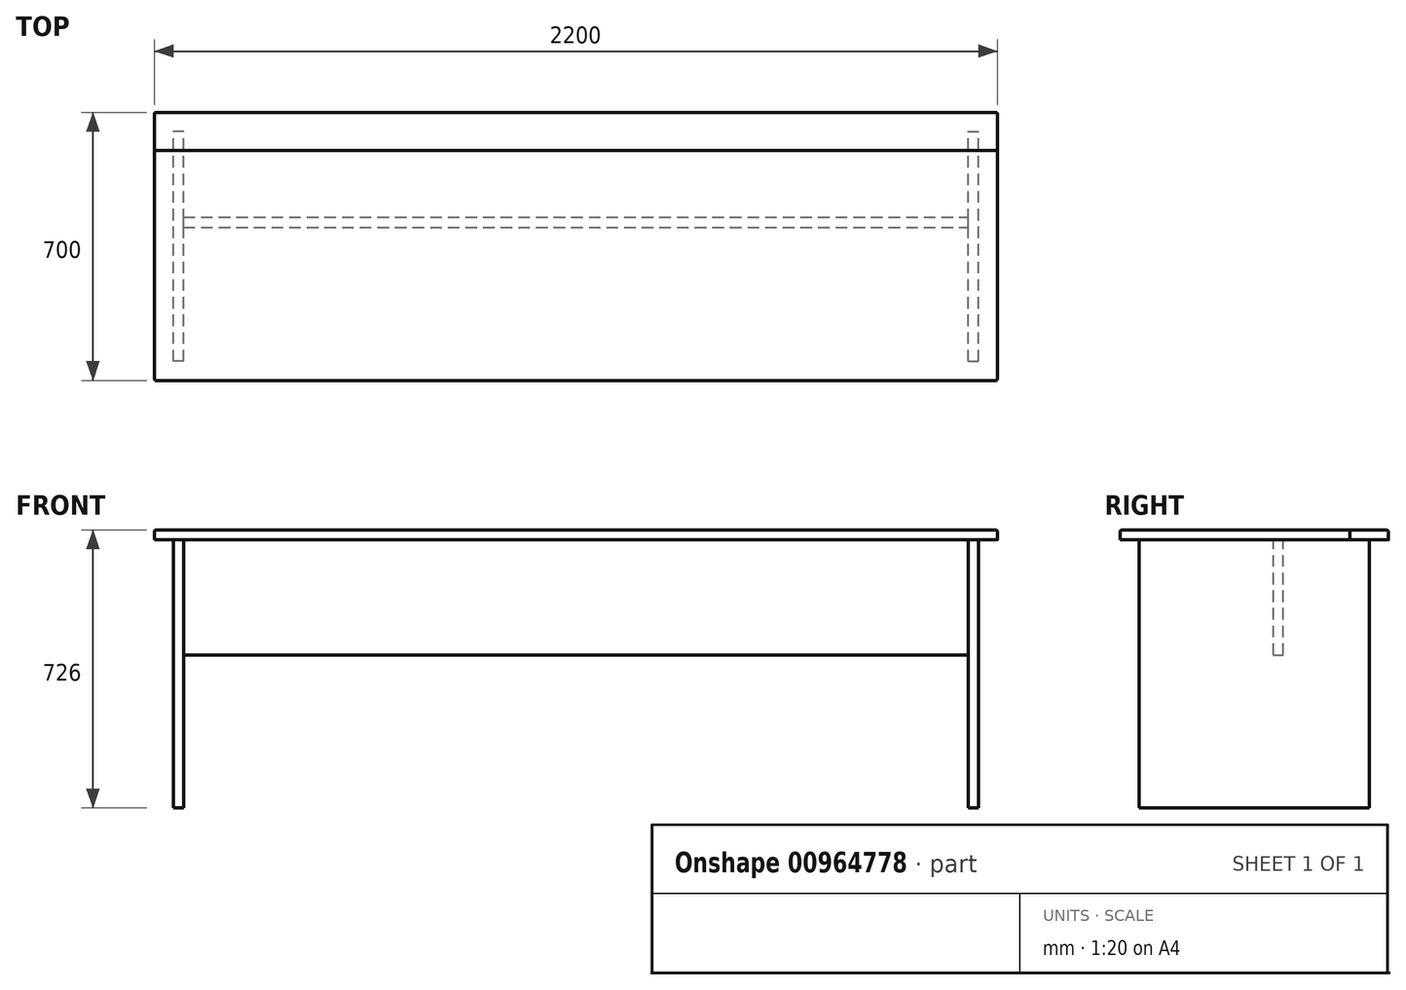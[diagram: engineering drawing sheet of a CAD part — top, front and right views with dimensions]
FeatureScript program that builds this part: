
annotation { "Feature Type Name" : "Feature", "Feature Type Description" : "" }
export const myFeature = defineFeature(function(context is Context, id is Id, definition is map)
    precondition{}
    {
        {
            var Q0;
            Q0=qCreatedBy(makeId("Top.planeOp"),FACE);
            var sketch = newSketch(context, id + "F0", { "sketchPlane" : qUnion([Q0])});
            skLineSegment(sketch, "E0.bottom", {"start": v(0, 0) * mm, "end": v(2200, 0) * mm});
            skLineSegment(sketch, "E0.top", {"start": v(0, 600) * mm, "end": v(2200, 600) * mm});
            skLineSegment(sketch, "E0.left", {"start": v(0, 0) * mm, "end": v(0, 600) * mm});
            skLineSegment(sketch, "E0.right", {"start": v(2200, 0) * mm, "end": v(2200, 600) * mm});
            skLineSegment(sketch, "E1.top", {"start": v(0, 700) * mm, "end": v(2200, 700) * mm});
            skLineSegment(sketch, "E1.left", {"start": v(0, 600) * mm, "end": v(0, 700) * mm});
            skLineSegment(sketch, "E1.right", {"start": v(2200, 600) * mm, "end": v(2200, 700) * mm});
            skSolve(sketch);
        }
        {
            var Q0;
            Q0=makeQuery(id+"F0.imprint","IMPRINT",FACE,{"disambiguationData":[TD([[makeQuery(id+"F0.imprint","IMPRINT",EDGE,{"derivedFrom":sQuery(id+"F0.wireOp",EDGE,"E0.bottom")}),1.0]])]});
            extrude(context, id + "F1", {"entities" : qUnion([Q0]), "oppositeDirection" : true, "depth" : 26 * mm, "offsetDistance" : 25 * mm});
        }
        {
            var Q0;
            Q0=makeQuery(id+"F0.imprint","IMPRINT",FACE,{"disambiguationData":[TD([[makeQuery(id+"F0.imprint","IMPRINT",EDGE,{"derivedFrom":sQuery(id+"F0.wireOp",EDGE,"E0.top")}),1.0]])]});
            extrude(context, id + "F2", {"entities" : qUnion([Q0]), "oppositeDirection" : true, "depth" : 26 * mm, "offsetDistance" : 25 * mm});
        }
        {
            var Q0;
            Q0=makeQuery(id+"F1.opExtrude","CAP_FACE",FACE,{"disambiguationData":[OSD([sQuery(id+"F0.wireOp",EDGE,"E0.bottom"),sQuery(id+"F0.wireOp",EDGE,"E0.left"),sQuery(id+"F0.wireOp",EDGE,"E0.right"),sQuery(id+"F0.wireOp",EDGE,"E0.top")])],"isStart":false});
            var sketch = newSketch(context, id + "F3", { "sketchPlane" : qUnion([Q0])});
            skLineSegment(sketch, "E2.0.0", {"start": v(0, -600) * mm, "end": v(2200, -600) * mm, "construction": true});
            skLineSegment(sketch, "E2.0.1", {"start": v(0, 0) * mm, "end": v(0, -600) * mm, "construction": true});
            skLineSegment(sketch, "E2.0.2", {"start": v(2200, 0) * mm, "end": v(0, 0) * mm, "construction": true});
            skLineSegment(sketch, "E2.0.3", {"start": v(2200, -600) * mm, "end": v(2200, 0) * mm, "construction": true});
            skLineSegment(sketch, "E3.0.0", {"start": v(0, -700) * mm, "end": v(2200, -700) * mm, "construction": true});
            skLineSegment(sketch, "E3.0.1", {"start": v(0, -600) * mm, "end": v(0, -700) * mm, "construction": true});
            skLineSegment(sketch, "E3.0.2", {"start": v(2200, -600) * mm, "end": v(0, -600) * mm, "construction": true});
            skLineSegment(sketch, "E3.0.3", {"start": v(2200, -700) * mm, "end": v(2200, -600) * mm, "construction": true});
            skLineSegment(sketch, "E4.bottom", {"start": v(76, -650) * mm, "end": v(50, -650) * mm});
            skLineSegment(sketch, "E4.top", {"start": v(76, -50) * mm, "end": v(50, -50) * mm});
            skLineSegment(sketch, "E4.left", {"start": v(50, -50) * mm, "end": v(50, -650) * mm});
            skLineSegment(sketch, "E4.right", {"start": v(76, -50) * mm, "end": v(76, -650) * mm});
            skLineSegment(sketch, "E5.bottom", {"start": v(2124, -650) * mm, "end": v(2150, -650) * mm});
            skLineSegment(sketch, "E5.top", {"start": v(2124, -50) * mm, "end": v(2150, -50) * mm});
            skLineSegment(sketch, "E5.left", {"start": v(2150, -50) * mm, "end": v(2150, -650) * mm});
            skLineSegment(sketch, "E5.right", {"start": v(2124, -50) * mm, "end": v(2124, -650) * mm});
            skLineSegment(sketch, "E6.bottom", {"start": v(76, -400) * mm, "end": v(2124, -400) * mm});
            skLineSegment(sketch, "E6.top", {"start": v(76, -426) * mm, "end": v(2124, -426) * mm});
            skLineSegment(sketch, "E6.left", {"start": v(2124, -400) * mm, "end": v(2124, -426) * mm});
            skLineSegment(sketch, "E6.right", {"start": v(76, -400) * mm, "end": v(76, -426) * mm});
            skSolve(sketch);
        }
        {
            var Q0;
            {var subQ5=sQuery(id+"F3.wireOp",EDGE,"E5.top");Q0=makeQuery(id+"F3.imprint","IMPRINT",FACE,{"disambiguationData":[TD([[makeQuery(id+"F3.imprint","IMPRINT",EDGE,{"derivedFrom":subQ5}),-1.0]])]});}
            var Q1;
            {var subQ0=sQuery(id+"F3.wireOp",EDGE,"E5.bottom");Q1=makeQuery(id+"F3.imprint","IMPRINT",FACE,{"disambiguationData":[TD([[makeQuery(id+"F3.imprint","IMPRINT",EDGE,{"derivedFrom":subQ0}),1.0]])]});}
            var Q2;
            {var subQ5=sQuery(id+"F3.wireOp",EDGE,"E4.top");Q2=makeQuery(id+"F3.imprint","IMPRINT",FACE,{"disambiguationData":[TD([[makeQuery(id+"F3.imprint","IMPRINT",EDGE,{"derivedFrom":subQ5}),1.0]])]});}
            var Q3;
            {var subQ0=sQuery(id+"F3.wireOp",EDGE,"E4.bottom");Q3=makeQuery(id+"F3.imprint","IMPRINT",FACE,{"disambiguationData":[TD([[makeQuery(id+"F3.imprint","IMPRINT",EDGE,{"derivedFrom":subQ0}),-1.0]])]});}
            extrude(context, id + "F4", {"entities" : qUnion([Q0, Q1, Q2, Q3]), "depth" : 700 * mm, "offsetDistance" : 25 * mm});
        }
        {
            var Q0;
            Q0=makeQuery(id+"F3.imprint","IMPRINT",FACE,{"disambiguationData":[TD([[makeQuery(id+"F3.imprint","IMPRINT",EDGE,{"derivedFrom":sQuery(id+"F3.wireOp",EDGE,"E6.bottom")}),-1.0]])]});
            extrude(context, id + "F5", {"entities" : qUnion([Q0]), "depth" : 300 * mm, "offsetDistance" : 25 * mm});
        }
        {
            var Q0;
            Q0=makeQuery(id+"F1.opExtrude","CAP_EDGE",EDGE,{"disambiguationData":[OSD([sQuery(id+"F0.wireOp",EDGE,"E0.bottom")])],"isStart":true});
            var Q1;
            Q1=makeQuery(id+"F1.opExtrude","SWEPT_EDGE",EDGE,{"disambiguationData":[OSD([sQuery(id+"F0.wireOp",EDGE,"E0.bottom"),sQuery(id+"F0.wireOp",EDGE,"E0.left")])]});
            var Q2;
            Q2=makeQuery(id+"F1.opExtrude","CAP_EDGE",EDGE,{"disambiguationData":[OSD([sQuery(id+"F0.wireOp",EDGE,"E0.left")])],"isStart":true});
            var Q3;
            Q3=makeQuery(id+"F1.opExtrude","SWEPT_EDGE",EDGE,{"disambiguationData":[OSD([sQuery(id+"F0.wireOp",EDGE,"E0.bottom"),sQuery(id+"F0.wireOp",EDGE,"E0.right")])]});
            var Q4;
            Q4=makeQuery(id+"F1.opExtrude","CAP_EDGE",EDGE,{"disambiguationData":[OSD([sQuery(id+"F0.wireOp",EDGE,"E0.right")])],"isStart":true});
            var Q5;
            Q5=makeQuery(id+"F2.opExtrude","CAP_EDGE",EDGE,{"disambiguationData":[OSD([sQuery(id+"F0.wireOp",EDGE,"E1.right")])],"isStart":true});
            var Q6;
            Q6=makeQuery(id+"F2.opExtrude","CAP_EDGE",EDGE,{"disambiguationData":[OSD([sQuery(id+"F0.wireOp",EDGE,"E1.left")])],"isStart":true});
            var Q7;
            Q7=makeQuery(id+"F2.opExtrude","CAP_EDGE",EDGE,{"disambiguationData":[OSD([sQuery(id+"F0.wireOp",EDGE,"E1.top")])],"isStart":true});
            var Q8;
            Q8=makeQuery(id+"F2.opExtrude","SWEPT_EDGE",EDGE,{"disambiguationData":[OSD([sQuery(id+"F0.wireOp",EDGE,"E1.top"),sQuery(id+"F0.wireOp",EDGE,"E1.right")])]});
            var Q9;
            Q9=makeQuery(id+"F2.opExtrude","SWEPT_EDGE",EDGE,{"disambiguationData":[OSD([sQuery(id+"F0.wireOp",EDGE,"E1.top"),sQuery(id+"F0.wireOp",EDGE,"E1.left")])]});
            fillet(context, id + "F6", {"entities" : qUnion([Q0, Q1, Q2, Q3, Q4, Q5, Q6, Q7, Q8, Q9]), "radius" : 5 * mm, "tangentPropagation" : true, "allowEdgeOverflow" : false});
        }
    });
